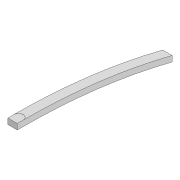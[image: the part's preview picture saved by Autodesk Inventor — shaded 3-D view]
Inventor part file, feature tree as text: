
AUTODESK INVENTOR PART (.ipt)
format: ipt  version: 2022 (Build 260153000, 153)  size: 128,512 bytes
history: native  units: mm
features: extrude x3, sketch x3, projected_geometry x2, fillet x1
ambient origin geometry x8: Origin, YZ Plane, XZ Plane, XY Plane, X Axis, Y Axis, Z Axis, Center Point
bodies: Solid1 (feature_tree)
feature tree (9):
  extrude  "Extrusion1"  Depth=10.0mm
  extrude  "Extrusion2"  Depth=40.0mm
  fillet  "Fillet1"  Radius=140.0mm
  extrude  "Extrusion3"  Depth=10.0mm TaperAngle=0.0deg
  sketch  "Sketch1"  dims[d0=180.0mm d1=10.0mm]
  sketch  "Sketch2"  dims[d2=3.3mm d3=40.0mm d5=140.0mm]
  projected_geometry  "Projected Loop1"
  projected_geometry  "Projected Loop2"
  sketch  "Sketch3"  dims[d6=3.3mm d7=6.0mm d8=0.0mm d9=6.0mm d10=498.004mm d11=90.0mm d12=10.0mm d13=0.0mm d14=2.0mm d15=100.0mm d16=0.0mm]
